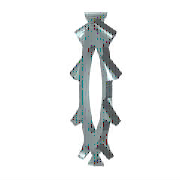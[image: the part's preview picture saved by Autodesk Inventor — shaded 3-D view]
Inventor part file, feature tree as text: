
AUTODESK INVENTOR PART (.ipt)
format: ipt  version: 2015 (Build 190159000, 159)  size: 159,744 bytes
history: native  units: mm (DEFAULTED — no unit token found)
features: sketch x2, extrude x1, pattern_circular x1, other x1, plane x1
ambient origin geometry x7: Origin, YZ Plane, XY Plane, X Axis, Y Axis, Z Axis, Center Point
bodies: Solid1 (feature_tree), Body (feature_tree)
feature tree (6):
  extrude  "Cut"  Depth=3.5814mm
  pattern_circular  "Cuts"  [2 undecoded]
  other  "Work Axis1"
  plane  "Work Plane1"
  sketch  "Sketch1"  dims[d0=8.128mm d1=3.5814mm]
  sketch  "Sketch2"  dims[d2=0.5588mm d3=0.0mm d4=30.0deg d5=5.8547mm d6=0.5588mm d7=0.0mm d8=0.12192mm d9=60.0mm d11=360.0deg d12=0.0mm d13=0.0mm d14=0.0mm d15=0.0mm d16=90.0deg]
note: 2 required parameter values undecoded (feature->parameter linkage not recoverable at this tier; creation-order binding heuristic only, values carry confidence <= 0.55)
